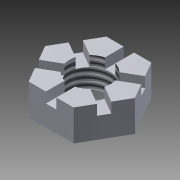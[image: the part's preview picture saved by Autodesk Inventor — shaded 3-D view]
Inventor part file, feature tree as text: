
AUTODESK INVENTOR PART (.ipt)
format: ipt  version: 2015 (Build 190159000, 159)  size: 119,296 bytes
history: native  units: mm
features: extrude x2, sketch x2, thread x1, pattern_circular x1
ambient origin geometry x8: Origin, YZ Plane, XZ Plane, XY Plane, X Axis, Y Axis, Z Axis, Center Point
bodies: Body1 (feature_tree)
feature tree (6):
  extrude  "拉伸2"  Depth=15.0mm
  thread  "螺纹1"  [1 undecoded]
  extrude  "拉伸3"  Depth=10.0mm TaperAngle=0.0deg
  pattern_circular  "环形阵列1"  [2 undecoded]
  sketch  "草图2"  dims[d6=3.444433mm d7=15.0mm d8=8.0mm]
  sketch  "草图3"  dims[d9=6.0mm d10=0.0mm d11=10.0mm d12=0.0mm d13=2.0mm d14=1.0mm d15=15.0mm d16=2.0mm d17=0.0mm d18=30.0mm d19=360.0deg]
note: 3 required parameter values undecoded (feature->parameter linkage not recoverable at this tier; creation-order binding heuristic only, values carry confidence <= 0.55)
